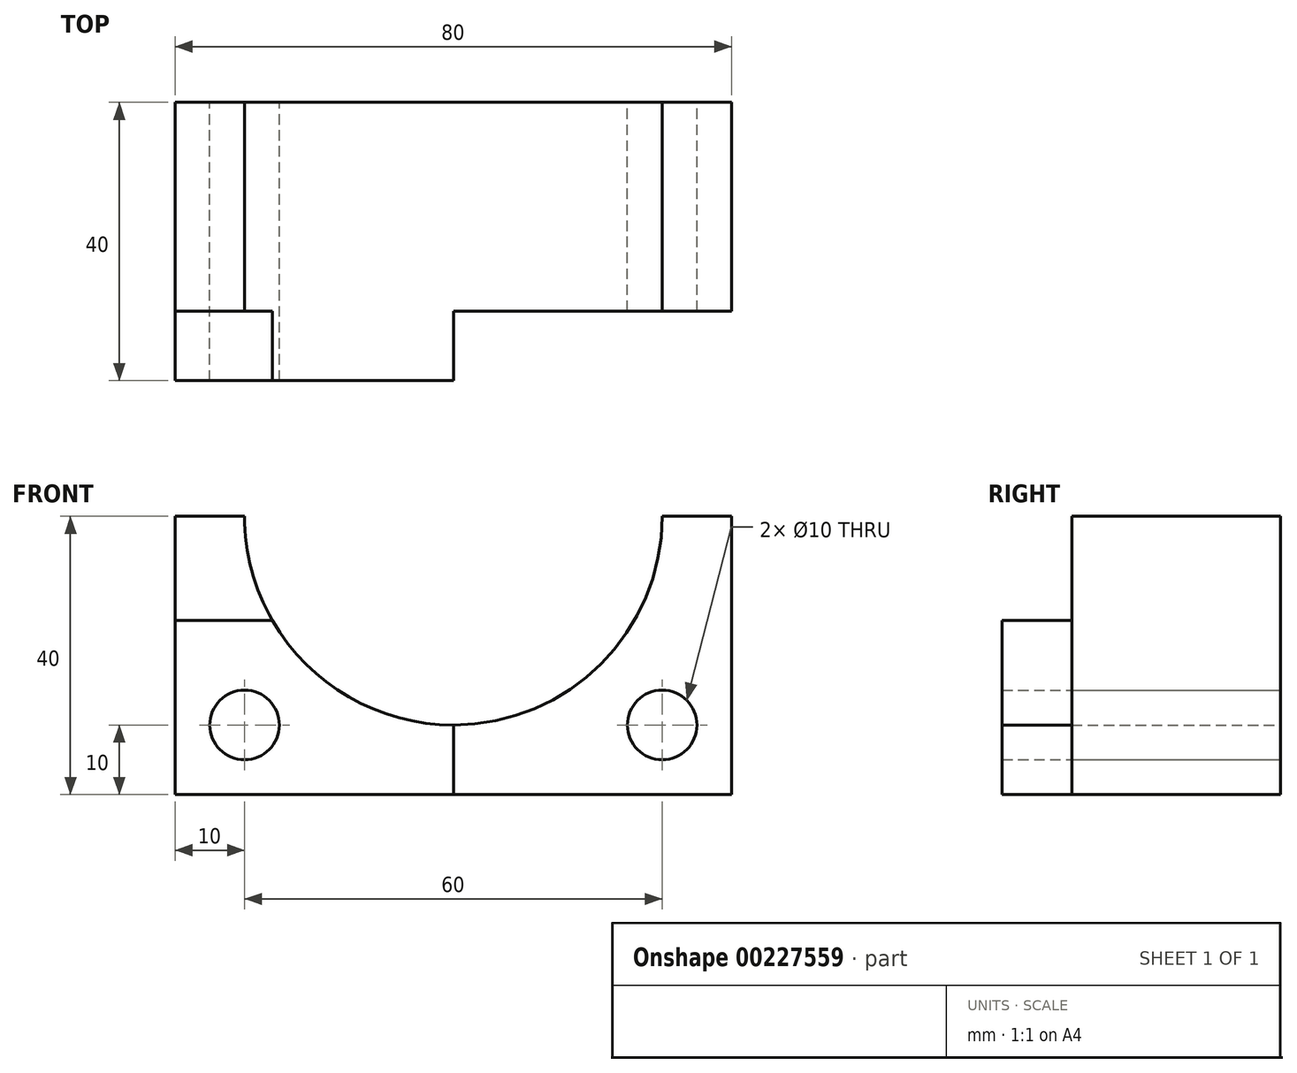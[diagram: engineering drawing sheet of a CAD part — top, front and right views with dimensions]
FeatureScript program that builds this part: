
annotation { "Feature Type Name" : "Feature", "Feature Type Description" : "" }
export const myFeature = defineFeature(function(context is Context, id is Id, definition is map)
    precondition{}
    {
        {
            var Q0;
            Q0=qCreatedBy(makeId("Front.planeOp"),FACE);
            var sketch = newSketch(context, id + "F0", { "sketchPlane" : qUnion([Q0])});
            skLineSegment(sketch, "E0", {"start": v(0, 10) * mm, "end": v(0, 0) * mm});
            skLineSegment(sketch, "E1", {"start": v(0, 0) * mm, "end": v(40, 0) * mm});
            skLineSegment(sketch, "E2", {"start": v(40, 0) * mm, "end": v(40, 40) * mm});
            skLineSegment(sketch, "E3", {"start": v(40, 40) * mm, "end": v(30, 40) * mm});
            skArc(sketch, "E4", {"start": v(0, 10) * mm, "mid": v(21.21, 18.79) * mm, "end": v(30, 40) * mm});
            skPoint(sketch, "E5.orphan", {"position": v(-30, 40) * mm});
            skCircle(sketch, "E6", {"center": v(30, 10) * mm, "radius": 5 * mm});
            skLineSegment(sketch, "E7.MirrorCS", {"start": v(-40, 40) * mm, "end": v(-30, 40) * mm});
            skLineSegment(sketch, "E8.MirrorCS", {"start": v(0, 0) * mm, "end": v(-40, 0) * mm});
            skCircle(sketch, "E9.MirrorC", {"center": v(-30, 10) * mm, "radius": 5 * mm});
            skLineSegment(sketch, "E10.MirrorCS", {"start": v(-40, 0) * mm, "end": v(-40, 40) * mm});
            skArc(sketch, "E11.MirrorCS", {"start": v(0, 10) * mm, "mid": v(-21.21, 18.79) * mm, "end": v(-30, 40) * mm});
            skLineSegment(sketch, "E12", {"start": v(-40, 25) * mm, "end": v(-25.98, 25) * mm});
            skSolve(sketch);
        }
        {
            var Q0;
            {var subQ0=sQuery(id+"F0.wireOp",EDGE,"E7.MirrorCS");Q0=makeQuery(id+"F0.imprint","IMPRINT",FACE,{"disambiguationData":[TD([[makeQuery(id+"F0.imprint","IMPRINT",EDGE,{"derivedFrom":subQ0}),-1.0]])]});}
            var Q1;
            Q1=makeQuery(id+"F0.imprint","IMPRINT",FACE,{"disambiguationData":[TD([[makeQuery(id+"F0.imprint","IMPRINT",EDGE,{"derivedFrom":sQuery(id+"F0.wireOp",EDGE,"E1")}),1.0]])]});
            extrude(context, id + "F1", {"entities" : qUnion([Q0, Q1]), "depth" : 30 * mm});
        }
        {
            var Q0;
            {var subQ1=sQuery(id+"F0.wireOp",EDGE,"E8.MirrorCS");Q0=makeQuery(id+"F0.imprint","IMPRINT",FACE,{"disambiguationData":[TD([[makeQuery(id+"F0.imprint","IMPRINT",EDGE,{"derivedFrom":subQ1}),-1.0]])]});}
            extrude(context, id + "F2", {"entities" : qUnion([Q0]), "operationType" : NewBodyOperationType.ADD, "depth" : 40 * mm});
        }
    });
